# Revit family: 49248
name_source: partatom
category: Lighting Fixtures
revit_build: Autodesk Revit 2018 (Build: 20170223_1515(x64)
units: mm (PartAtom-declared; Revit-internal decimal feet)

## family parameters
Cut with Voids When Loaded = No
Host = Face
Light Source = Yes
OmniClass Number = 23.80.70.00
OmniClass Title = Lighting
Part Type = Normal
Room Calculation Point = No
Round Connector Dimension = Use Diameter
Shared = No

## types (1)
- 0049248 START SURFACE IP66 1500LM 840 DA BLK
    Apparent Load = 14 VA
    Assembly Code = D5020200
    AssetType = Fixed
    ClassificationName = Uniclass2015
    ClassificationValue = EF_70_80
    Color Filter = 16777215
    Cost = 0 $
    Default Elevation = 1219 mm
    Description = LED exterior surface mounted luminaire, 350mm diameter, 1500lm as max. lumen output, 15W max. power consumption, 100lm/W efficacy, 4000K color temperature, CRI80, IP66, IK10, 60,000 hours (L70), black housing, vandal resistant. DALI and DALI 2 dimming compatibility, supplied with anti-theft screws
    Dimming Lamp Color Temperature Shift = <None>
    DocumentationLiterature = http://www.sylvania-lighting.com
    DurationUnit = hours
    ElectricShockClassification = 111
    Emit Shape Visible in Rendering = No
    Emit from Circle Diameter = 200 mm  [stored 0.656168 ft]
    ExpectedLife = 50000
    HoleAngle_SYL = 45.00°
    HoleHoleRad_SYL = 6 mm  [stored 0.019685 ft]
    HoleRad_SYL = 134 mm
    IfcExportAs = Class II
    IfcExportType = IfcLightFixtureType
    ImpactProtectionIndex = IfcLightFixtureType
    IngressProtection = IfcLightFixtureType
    InputNominalFrequency = 4000
    InputVoltage = 0
    LampColourRenderingIndex = 16500
    LampColourTemperature = LED
    LampMacAdamStep = 80
    LampNominalLuminous = 4000 K
    LightOutputRatio = LED
    LuminaireType = 0
    ManufacturerName = 111 lm/W
    Material = Feilo Sylvania
    Material_1_SYL = Body-Sylvania-StartSurfaceIP66-Black
    Material_2_SYL = Diffuser-Sylvania-StartSurfaceIP66
    Material_3_SYL = LED-Sylvania-StartSurfaceIP66
    Model = START SURFACE IP66 1500LM 840 IK10 DALI BLK
    ModelNumber = 0049248
    ModelReference = START SURFACE IP66 1500LM 840 IK10 DALI BLK
    Name = START SURFACE IP66 1500LM 840 IK10 DALI BLK
    NominalDepth = 300 mm
    NominalHeight = 90 mm  [stored 0.295276 ft]
    NominalLength = 350 mm  [stored 1.14829 ft]
    Photometric Web File = 0049248.ies
    PowerConsumption = Lighting
    PowerFactor = 0
    Tilt Angle = -90.00°
    Type Image = <None>
    TypeName = START SURFACE IP66 1500LM 840 IK10 DALI BLK
    URL = 1
    Voltage = 0 V
    WarrantyDescription = http://www.sylvania-lighting.com

note: [stored X ft] marks values corroborated as IEEE doubles in the binary element streams (Revit-internal decimal feet)

## geometry (parser evidence)
native form markers: Sweep x3
no freeform markers — native parametric forms only
